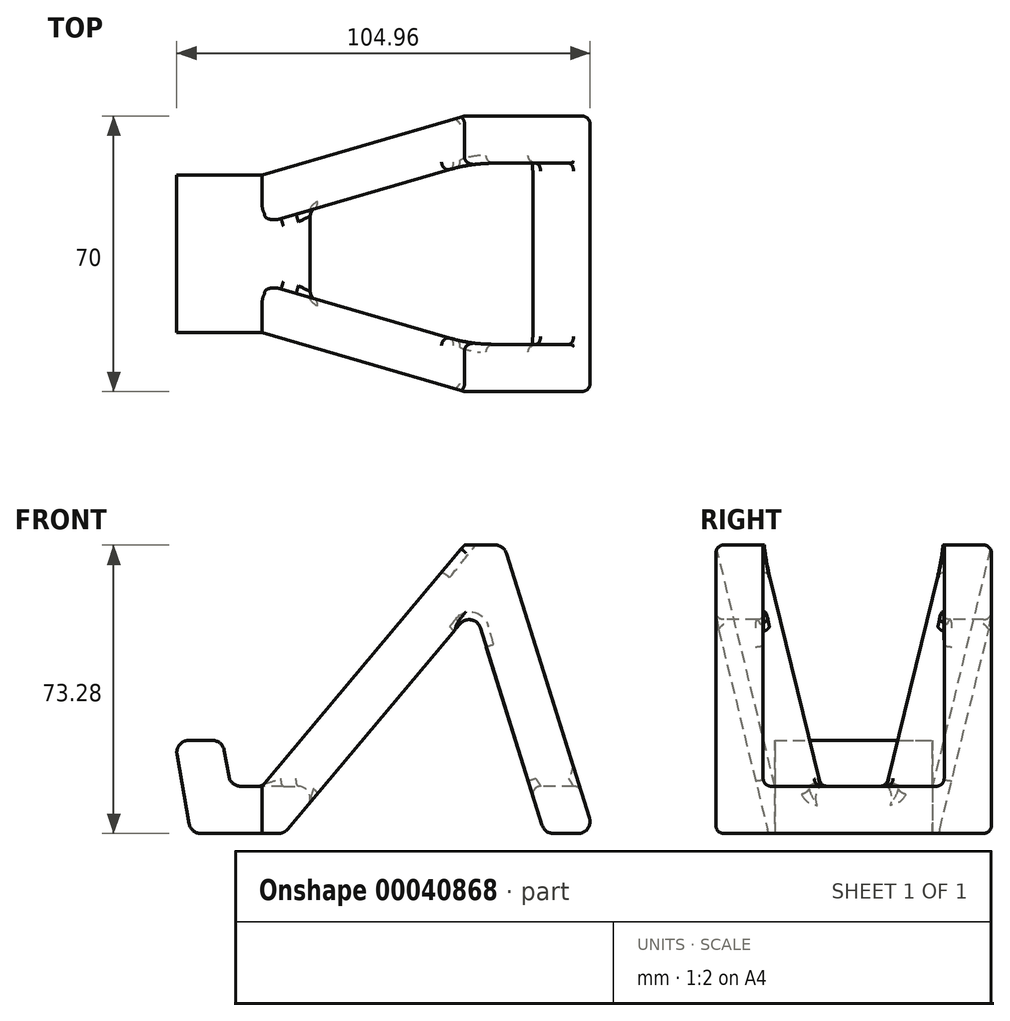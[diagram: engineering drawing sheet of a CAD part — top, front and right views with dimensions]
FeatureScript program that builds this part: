
annotation { "Feature Type Name" : "Feature", "Feature Type Description" : "" }
export const myFeature = defineFeature(function(context is Context, id is Id, definition is map)
    precondition{}
    {
        {
            var Q0;
            Q0=qCreatedBy(makeId("Front.planeOp"),FACE);
            var sketch = newSketch(context, id + "F0", { "sketchPlane" : qUnion([Q0])});
            skLineSegment(sketch, "E0", {"start": v(0, 0) * mm, "end": v(-23.66, 0) * mm});
            skLineSegment(sketch, "E1", {"start": v(-23.66, 0) * mm, "end": v(-27.83, 23.64) * mm});
            skLineSegment(sketch, "E2", {"start": v(-27.83, 23.64) * mm, "end": v(-15.65, 23.64) * mm});
            skLineSegment(sketch, "E3", {"start": v(-15.65, 23.64) * mm, "end": v(-13.6, 12) * mm});
            skLineSegment(sketch, "E4", {"start": v(-13.6, 12) * mm, "end": v(-5.6, 12) * mm});
            skLineSegment(sketch, "E5", {"start": v(-5.6, 12) * mm, "end": v(45.83, 73.28) * mm});
            skLineSegment(sketch, "E6", {"start": v(45.83, 73.28) * mm, "end": v(55.83, 73.28) * mm});
            skLineSegment(sketch, "E7", {"start": v(55.83, 73.28) * mm, "end": v(78.79, 0) * mm});
            skLineSegment(sketch, "E8", {"start": v(78.79, 0) * mm, "end": v(66.21, 0) * mm});
            skLineSegment(sketch, "E9", {"start": v(66.21, 0) * mm, "end": v(48.21, 57.46) * mm});
            skLineSegment(sketch, "E10", {"start": v(48.21, 57.46) * mm, "end": v(0, 0) * mm});
            skSolve(sketch);
        }
        {
            var Q0;
            Q0=makeQuery(id+"F0.imprint","IMPRINT",FACE,{"disambiguationData":[TD([[makeQuery(id+"F0.imprint","IMPRINT",EDGE,{"derivedFrom":sQuery(id+"F0.wireOp",EDGE,"E0")}),-1.0]])]});
            extrude(context, id + "F1", {"entities" : qUnion([Q0]), "endBound" : BoundingType.SYMMETRIC, "depth" : 70 * mm});
        }
        {
            var Q0;
            Q0=qCreatedBy(makeId("Top.planeOp"),FACE);
            var sketch = newSketch(context, id + "F2", { "sketchPlane" : qUnion([Q0])});
            skLineSegment(sketch, "E11", {"start": v(-5.6, 20) * mm, "end": v(45.83, 35) * mm});
            skLineSegment(sketch, "E12", {"start": v(45.83, -35) * mm, "end": v(-5.6, -20) * mm});
            skLineSegment(sketch, "E13", {"start": v(-5.6, -20) * mm, "end": v(-27.83, -20) * mm});
            skLineSegment(sketch, "E14", {"start": v(-27.83, -20) * mm, "end": v(-27.83, 20) * mm});
            skLineSegment(sketch, "E15", {"start": v(-27.83, 20) * mm, "end": v(-5.6, 20) * mm});
            skLineSegment(sketch, "E16", {"start": v(45.83, 35) * mm, "end": v(78.79, 35) * mm});
            skLineSegment(sketch, "E17", {"start": v(78.79, 35) * mm, "end": v(78.79, -35) * mm});
            skLineSegment(sketch, "E18", {"start": v(78.79, -35) * mm, "end": v(45.83, -35) * mm});
            skPoint(sketch, "E19", {"position": v(-27.83, 0) * mm});
            skPoint(sketch, "E20", {"position": v(78.79, 0) * mm});
            skSolve(sketch);
        }
        {
            var Q0;
            Q0 = qSketchRegion(id + "F2", true);
            extrude(context, id + "F3", {"entities" : qUnion([Q0]), "operationType" : NewBodyOperationType.INTERSECT, "endBound" : BoundingType.THROUGH_ALL, "depth" : 25 * mm});
        }
        {
            var Q0;
            Q0=makeQuery(id+"F1.opExtrude","SWEPT_FACE",FACE,{"disambiguationData":[OSD([sQuery(id+"F0.wireOp",EDGE,"E4")])]});
            var sketch = newSketch(context, id + "F4", { "sketchPlane" : qUnion([Q0])});
            skLineSegment(sketch, "E21", {"start": v(-5.6, 7.5) * mm, "end": v(-5.6, -7.5) * mm});
            skLineSegment(sketch, "E22", {"start": v(-5.6, -7.5) * mm, "end": v(47.54, -23) * mm});
            skLineSegment(sketch, "E23", {"start": v(47.54, -23) * mm, "end": v(87.54, -23) * mm});
            skLineSegment(sketch, "E24", {"start": v(87.54, -23) * mm, "end": v(87.54, 23) * mm});
            skLineSegment(sketch, "E25", {"start": v(87.54, 23) * mm, "end": v(47.54, 23) * mm});
            skLineSegment(sketch, "E26", {"start": v(47.54, 23) * mm, "end": v(-5.6, 7.5) * mm});
            skPoint(sketch, "E27", {"position": v(87.54, 0) * mm});
            skSolve(sketch);
        }
        {
            var Q0;
            Q0 = qSketchRegion(id + "F4", true);
            extrude(context, id + "F5", {"entities" : qUnion([Q0]), "operationType" : NewBodyOperationType.REMOVE, "endBound" : BoundingType.THROUGH_ALL, "depth" : 25 * mm});
        }
        {
            var Q0;
            Q0=makeQuery(id+"F1.opExtrude","SWEPT_EDGE",EDGE,{"disambiguationData":[OSD([sQuery(id+"F0.wireOp",EDGE,"E3"),sQuery(id+"F0.wireOp",EDGE,"E4")])]});
            var Q1;
            Q1=makeQuery(id+"F1.opExtrude","SWEPT_EDGE",EDGE,{"disambiguationData":[OSD([sQuery(id+"F0.wireOp",EDGE,"E0"),sQuery(id+"F0.wireOp",EDGE,"E1")])]});
            var Q2;
            Q2=makeQuery(id+"F1.opExtrude","SWEPT_EDGE",EDGE,{"disambiguationData":[OSD([sQuery(id+"F0.wireOp",EDGE,"E7"),sQuery(id+"F0.wireOp",EDGE,"E8")])]});
            var Q3;
            Q3=makeQuery(id+"F1.opExtrude","SWEPT_EDGE",EDGE,{"disambiguationData":[OSD([sQuery(id+"F0.wireOp",EDGE,"E8"),sQuery(id+"F0.wireOp",EDGE,"E9")])]});
            var Q4;
            Q4=makeQuery(id+"F1.opExtrude","SWEPT_EDGE",EDGE,{"disambiguationData":[OSD([sQuery(id+"F0.wireOp",EDGE,"E0"),sQuery(id+"F0.wireOp",EDGE,"E10")])]});
            var Q5;
            Q5=makeQuery(id+"F5.boolean.opBoolean","INTERSECT",EDGE,{"derivedFrom":[makeQuery(id+"F1.opExtrude","SWEPT_FACE",FACE,{"disambiguationData":[OSD([sQuery(id+"F0.wireOp",EDGE,"E10")])]}),makeQuery(id+"F5.opExtrude","CAP_FACE",FACE,{"disambiguationData":[OSD([sQuery(id+"F4.wireOp",EDGE,"E21"),sQuery(id+"F4.wireOp",EDGE,"E22"),sQuery(id+"F4.wireOp",EDGE,"E23"),sQuery(id+"F4.wireOp",EDGE,"E24"),sQuery(id+"F4.wireOp",EDGE,"E25"),sQuery(id+"F4.wireOp",EDGE,"E26")])],"isStart":true})]});
            var Q6;
            {var subQ0=sQuery(id+"F0.wireOp",EDGE,"E5");var subQ1=sQuery(id+"F0.wireOp",EDGE,"E6");Q6=makeQuery(id+"F5.boolean.opBoolean","SPLIT",EDGE,{"disambiguationData":[TD([makeQuery(id+"F3.boolean.opBoolean","COPY",FACE,{"derivedFrom":makeQuery(id+"F3.boolean.toolComplement.opBoolean","COPY",FACE,{"derivedFrom":makeQuery(id+"F3.opExtrude","SWEPT_FACE",FACE,{"disambiguationData":[OSD([sQuery(id+"F2.wireOp",EDGE,"E11")])]})})})])],"derivedFrom":makeQuery(id+"F1.opExtrude","SWEPT_EDGE",EDGE,{"disambiguationData":[OSD([subQ0,subQ1])]})});}
            var Q7;
            {var subQ0=sQuery(id+"F0.wireOp",EDGE,"E6");var subQ1=sQuery(id+"F0.wireOp",EDGE,"E7");Q7=makeQuery(id+"F5.boolean.opBoolean","SPLIT",EDGE,{"disambiguationData":[TD([makeQuery(id+"F5.opExtrude","SWEPT_FACE",FACE,{"disambiguationData":[OSD([sQuery(id+"F4.wireOp",EDGE,"E25")])]})])],"derivedFrom":makeQuery(id+"F1.opExtrude","SWEPT_EDGE",EDGE,{"disambiguationData":[OSD([subQ0,subQ1])]})});}
            var Q8;
            {var subQ0=sQuery(id+"F0.wireOp",EDGE,"E6");var subQ1=sQuery(id+"F0.wireOp",EDGE,"E7");Q8=makeQuery(id+"F5.boolean.opBoolean","SPLIT",EDGE,{"disambiguationData":[TD([makeQuery(id+"F5.opExtrude","SWEPT_FACE",FACE,{"disambiguationData":[OSD([sQuery(id+"F4.wireOp",EDGE,"E23")])]})])],"derivedFrom":makeQuery(id+"F1.opExtrude","SWEPT_EDGE",EDGE,{"disambiguationData":[OSD([subQ0,subQ1])]})});}
            var Q9;
            {var subQ0=sQuery(id+"F0.wireOp",EDGE,"E5");var subQ1=sQuery(id+"F0.wireOp",EDGE,"E6");Q9=makeQuery(id+"F5.boolean.opBoolean","SPLIT",EDGE,{"disambiguationData":[TD([makeQuery(id+"F3.boolean.opBoolean","COPY",FACE,{"derivedFrom":makeQuery(id+"F3.boolean.toolComplement.opBoolean","COPY",FACE,{"derivedFrom":makeQuery(id+"F3.opExtrude","SWEPT_FACE",FACE,{"disambiguationData":[OSD([sQuery(id+"F2.wireOp",EDGE,"E12")])]})})})])],"derivedFrom":makeQuery(id+"F1.opExtrude","SWEPT_EDGE",EDGE,{"disambiguationData":[OSD([subQ0,subQ1])]})});}
            var Q10;
            {var subQ0=sQuery(id+"F0.wireOp",EDGE,"E9");var subQ1=sQuery(id+"F0.wireOp",EDGE,"E10");Q10=makeQuery(id+"F5.boolean.opBoolean","SPLIT",EDGE,{"disambiguationData":[TD([makeQuery(id+"F5.opExtrude","SWEPT_FACE",FACE,{"disambiguationData":[OSD([sQuery(id+"F4.wireOp",EDGE,"E25")])]})])],"derivedFrom":makeQuery(id+"F1.opExtrude","SWEPT_EDGE",EDGE,{"disambiguationData":[OSD([subQ0,subQ1])]})});}
            var Q11;
            {var subQ0=sQuery(id+"F0.wireOp",EDGE,"E9");var subQ1=sQuery(id+"F0.wireOp",EDGE,"E10");Q11=makeQuery(id+"F5.boolean.opBoolean","SPLIT",EDGE,{"disambiguationData":[TD([makeQuery(id+"F5.opExtrude","SWEPT_FACE",FACE,{"disambiguationData":[OSD([sQuery(id+"F4.wireOp",EDGE,"E23")])]})])],"derivedFrom":makeQuery(id+"F1.opExtrude","SWEPT_EDGE",EDGE,{"disambiguationData":[OSD([subQ0,subQ1])]})});}
            var Q12;
            Q12=makeQuery(id+"F1.opExtrude","SWEPT_EDGE",EDGE,{"disambiguationData":[OSD([sQuery(id+"F0.wireOp",EDGE,"E1"),sQuery(id+"F0.wireOp",EDGE,"E2")])]});
            var Q13;
            Q13=makeQuery(id+"F1.opExtrude","SWEPT_EDGE",EDGE,{"disambiguationData":[OSD([sQuery(id+"F0.wireOp",EDGE,"E2"),sQuery(id+"F0.wireOp",EDGE,"E3")])]});
            fillet(context, id + "F6", {"entities" : qUnion([Q0, Q1, Q2, Q3, Q4, Q5, Q6, Q7, Q8, Q9, Q10, Q11, Q12, Q13]), "radius" : 3 * mm, "tangentPropagation" : true, "allowEdgeOverflow" : false});
        }
        {
            var Q0;
            Q0=makeQuery(id+"F5.boolean.opBoolean","COPY",EDGE,{"derivedFrom":makeQuery(id+"F5.opExtrude","SWEPT_EDGE",EDGE,{"disambiguationData":[OSD([sQuery(id+"F4.wireOp",EDGE,"E22"),sQuery(id+"F4.wireOp",EDGE,"E23")])]})});
            var Q1;
            Q1=makeQuery(id+"F5.boolean.opBoolean","COPY",EDGE,{"derivedFrom":makeQuery(id+"F5.opExtrude","SWEPT_EDGE",EDGE,{"disambiguationData":[OSD([sQuery(id+"F4.wireOp",EDGE,"E25"),sQuery(id+"F4.wireOp",EDGE,"E26")])]})});
            var Q2;
            Q2=makeQuery(id+"F3.boolean.opBoolean","COPY",EDGE,{"derivedFrom":makeQuery(id+"F3.boolean.toolComplement.opBoolean","COPY",EDGE,{"derivedFrom":makeQuery(id+"F3.opExtrude","SWEPT_EDGE",EDGE,{"disambiguationData":[OSD([sQuery(id+"F2.wireOp",EDGE,"E11"),sQuery(id+"F2.wireOp",EDGE,"E16")])]})})});
            var Q3;
            Q3=makeQuery(id+"F3.boolean.opBoolean","COPY",EDGE,{"derivedFrom":makeQuery(id+"F3.boolean.toolComplement.opBoolean","COPY",EDGE,{"derivedFrom":makeQuery(id+"F3.opExtrude","SWEPT_EDGE",EDGE,{"disambiguationData":[OSD([sQuery(id+"F2.wireOp",EDGE,"E12"),sQuery(id+"F2.wireOp",EDGE,"E18")])]})})});
            var Q4;
            Q4=makeQuery(id+"F3.boolean.opBoolean","COPY",EDGE,{"derivedFrom":makeQuery(id+"F3.boolean.toolComplement.opBoolean","COPY",EDGE,{"derivedFrom":makeQuery(id+"F3.opExtrude","SWEPT_EDGE",EDGE,{"disambiguationData":[OSD([sQuery(id+"F2.wireOp",EDGE,"E12"),sQuery(id+"F2.wireOp",EDGE,"E13")])]})})});
            var Q5;
            Q5=makeQuery(id+"F3.boolean.opBoolean","COPY",EDGE,{"derivedFrom":makeQuery(id+"F3.boolean.toolComplement.opBoolean","COPY",EDGE,{"derivedFrom":makeQuery(id+"F3.opExtrude","SWEPT_EDGE",EDGE,{"disambiguationData":[OSD([sQuery(id+"F2.wireOp",EDGE,"E11"),sQuery(id+"F2.wireOp",EDGE,"E15")])]})})});
            fillet(context, id + "F7", {"entities" : qUnion([Q0, Q1, Q2, Q3, Q4, Q5]), "radius" : 40 * mm, "tangentPropagation" : true, "allowEdgeOverflow" : false});
        }
        {
            var Q0;
            Q0=makeQuery(id+"F1.opExtrude","CAP_FACE",FACE,{"disambiguationData":[OSD([sQuery(id+"F0.wireOp",EDGE,"E0"),sQuery(id+"F0.wireOp",EDGE,"E1"),sQuery(id+"F0.wireOp",EDGE,"E2"),sQuery(id+"F0.wireOp",EDGE,"E3"),sQuery(id+"F0.wireOp",EDGE,"E4"),sQuery(id+"F0.wireOp",EDGE,"E5"),sQuery(id+"F0.wireOp",EDGE,"E6"),sQuery(id+"F0.wireOp",EDGE,"E7"),sQuery(id+"F0.wireOp",EDGE,"E8"),sQuery(id+"F0.wireOp",EDGE,"E9"),sQuery(id+"F0.wireOp",EDGE,"E10")])],"isStart":true});
            var Q1;
            Q1=makeQuery(id+"F1.opExtrude","CAP_FACE",FACE,{"disambiguationData":[OSD([sQuery(id+"F0.wireOp",EDGE,"E0"),sQuery(id+"F0.wireOp",EDGE,"E1"),sQuery(id+"F0.wireOp",EDGE,"E2"),sQuery(id+"F0.wireOp",EDGE,"E3"),sQuery(id+"F0.wireOp",EDGE,"E4"),sQuery(id+"F0.wireOp",EDGE,"E5"),sQuery(id+"F0.wireOp",EDGE,"E6"),sQuery(id+"F0.wireOp",EDGE,"E7"),sQuery(id+"F0.wireOp",EDGE,"E8"),sQuery(id+"F0.wireOp",EDGE,"E9"),sQuery(id+"F0.wireOp",EDGE,"E10")])],"isStart":false});
            fillet(context, id + "F8", {"entities" : qUnion([Q0, Q1]), "radius" : 2 * mm, "tangentPropagation" : true, "allowEdgeOverflow" : false});
        }
        {
            var Q0;
            Q0=makeQuery(id+"F5.boolean.opBoolean","COPY",FACE,{"derivedFrom":makeQuery(id+"F5.opExtrude","SWEPT_FACE",FACE,{"disambiguationData":[OSD([sQuery(id+"F4.wireOp",EDGE,"E26")])]})});
            var Q1;
            Q1=makeQuery(id+"F5.boolean.opBoolean","COPY",FACE,{"derivedFrom":makeQuery(id+"F5.opExtrude","SWEPT_FACE",FACE,{"disambiguationData":[OSD([sQuery(id+"F4.wireOp",EDGE,"E22")])]})});
            var Q2;
            Q2=makeQuery(id+"F5.boolean.opBoolean","COPY",FACE,{"derivedFrom":makeQuery(id+"F5.opExtrude","CAP_FACE",FACE,{"disambiguationData":[OSD([sQuery(id+"F4.wireOp",EDGE,"E21"),sQuery(id+"F4.wireOp",EDGE,"E22"),sQuery(id+"F4.wireOp",EDGE,"E23"),sQuery(id+"F4.wireOp",EDGE,"E24"),sQuery(id+"F4.wireOp",EDGE,"E25"),sQuery(id+"F4.wireOp",EDGE,"E26")])],"isStart":true})});
            fillet(context, id + "F9", {"entities" : qUnion([Q0, Q1, Q2]), "radius" : 2 * mm, "tangentPropagation" : true, "allowEdgeOverflow" : false});
        }
    });
